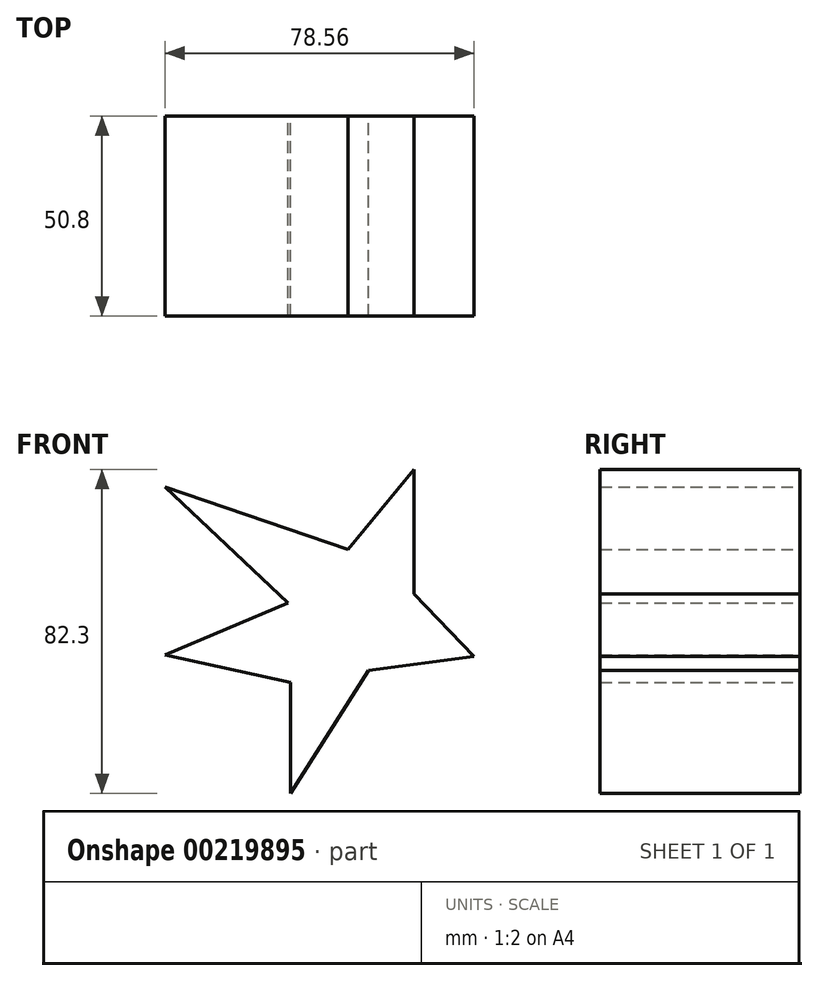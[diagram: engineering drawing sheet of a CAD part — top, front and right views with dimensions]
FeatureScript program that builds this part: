
annotation { "Feature Type Name" : "Feature", "Feature Type Description" : "" }
export const myFeature = defineFeature(function(context is Context, id is Id, definition is map)
    precondition{}
    {
        {
            var Q0;
            Q0=qCreatedBy(makeId("Front.planeOp"),FACE);
            var sketch = newSketch(context, id + "F0", { "sketchPlane" : qUnion([Q0])});
            skLineSegment(sketch, "E0", {"start": v(-17.91, 50.82) * mm, "end": v(-49.17, 37.54) * mm});
            skLineSegment(sketch, "E1", {"start": v(-49.17, 37.54) * mm, "end": v(-17.32, 30.6) * mm});
            skLineSegment(sketch, "E2", {"start": v(-17.32, 30.6) * mm, "end": v(-17.32, 2.39) * mm});
            skLineSegment(sketch, "E3", {"start": v(-17.32, 2.39) * mm, "end": v(2.58, 33.69) * mm});
            skLineSegment(sketch, "E4", {"start": v(2.58, 33.69) * mm, "end": v(29.39, 37.17) * mm});
            skLineSegment(sketch, "E5", {"start": v(29.39, 37.17) * mm, "end": v(14.13, 53.08) * mm});
            skLineSegment(sketch, "E6", {"start": v(14.13, 53.08) * mm, "end": v(14.13, 84.69) * mm});
            skLineSegment(sketch, "E7", {"start": v(14.13, 84.69) * mm, "end": v(-2.65, 64.42) * mm});
            skLineSegment(sketch, "E8", {"start": v(-2.65, 64.42) * mm, "end": v(-49.17, 80.3) * mm});
            skLineSegment(sketch, "E9", {"start": v(-49.17, 80.3) * mm, "end": v(-17.91, 50.82) * mm});
            skSolve(sketch);
        }
        {
            var Q0;
            Q0=makeQuery(id+"F0.imprint","IMPRINT",FACE,{"disambiguationData":[TD([[makeQuery(id+"F0.imprint","IMPRINT",EDGE,{"derivedFrom":sQuery(id+"F0.wireOp",EDGE,"E0")}),1.0]])]});
            extrude(context, id + "F1", {"entities" : qUnion([Q0]), "depth" : 50.8 * mm});
        }
    });
